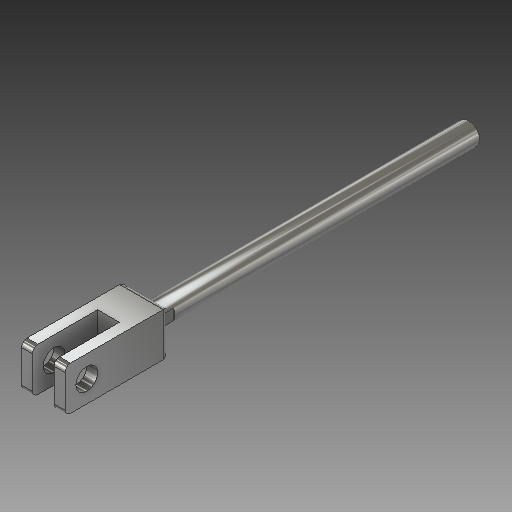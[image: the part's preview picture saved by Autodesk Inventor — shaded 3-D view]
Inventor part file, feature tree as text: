
AUTODESK INVENTOR PART (.ipt)
format: ipt  version: 2017 SP1 (Build 210196100, 196)  size: 164,864 bytes
history: native  units: in
note: dims shown in document units (in); Inventor stores cm internally (conversion verified against a paired STEP export)
features: extrude x5, sketch x5, fillet x1
ambient origin geometry x8: Origin, YZ Plane, XZ Plane, XY Plane, X Axis, Y Axis, Z Axis, Center Point
bodies: Solid1 (feature_tree)
feature tree (11):
  extrude  "Extrusion1"  Depth=3.5in TaperAngle=0.0deg
  extrude  "Extrusion2"  Depth=0.2in TaperAngle=0.0deg
  extrude  "Extrusion3"  Depth=0.44in TaperAngle=0.0deg
  extrude  "Extrusion4"  Depth=0.75in TaperAngle=0.0deg
  extrude  "Extrusion5"  Depth=0.25in
  fillet  "Fillet1"  Radius=0.75in
  sketch  "Sketch1"  dims[d0=0.25in d1=3.5in d2=0.0in]
  sketch  "Sketch2"  dims[d3=0.125in d4=0.2in d5=0.0in]
  sketch  "Sketch3"  dims[d6=0.5in d7=0.44in d8=0.0in]
  sketch  "Sketch4"  dims[d9=0.25in d10=0.75in d11=0.0in]
  sketch  "Sketch5"  dims[d12=0.25in d13=0.25in d14=0.75in d15=0.0in d16=0.0625in]
